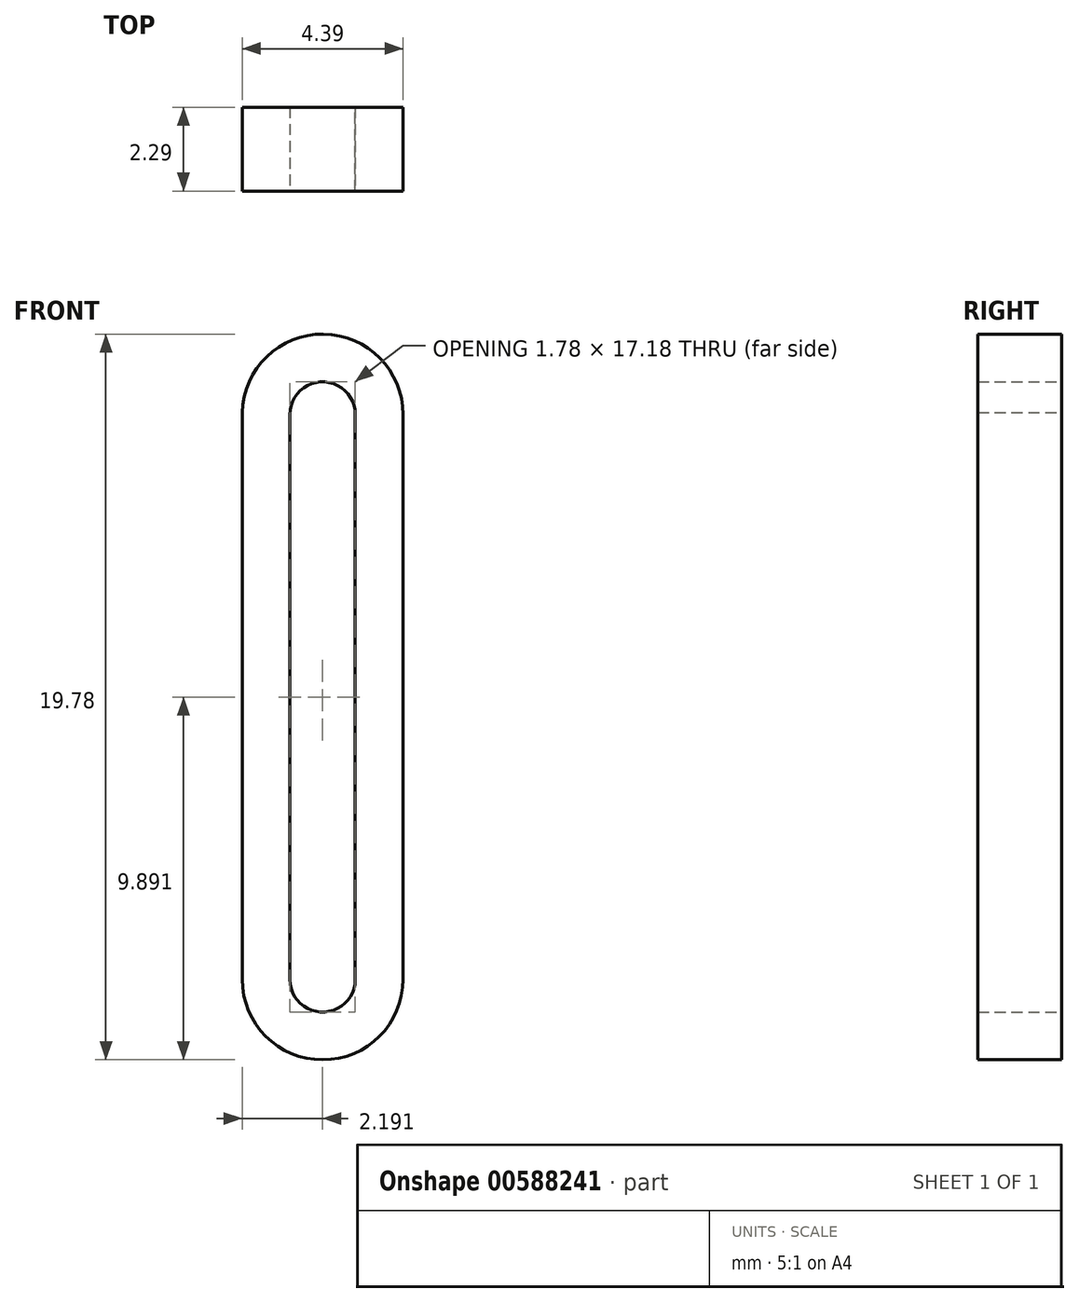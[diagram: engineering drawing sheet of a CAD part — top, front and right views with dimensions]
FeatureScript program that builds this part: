
annotation { "Feature Type Name" : "Feature", "Feature Type Description" : "" }
export const myFeature = defineFeature(function(context is Context, id is Id, definition is map)
    precondition{}
    {
        {
            var Q0;
            Q0=qCreatedBy(makeId("Front.planeOp"),FACE);
            var sketch = newSketch(context, id + "F0", { "sketchPlane" : qUnion([Q0])});
            skLineSegment(sketch, "E0", {"start": v(-49.36, 48.2) * mm, "end": v(-49.36, 32.75) * mm});
            skArc(sketch, "E1", {"start": v(-49.36, 32.75) * mm, "mid": v(-47.17, 30.56) * mm, "end": v(-44.97, 32.75) * mm});
            skLineSegment(sketch, "E2", {"start": v(-44.97, 32.75) * mm, "end": v(-44.97, 48.15) * mm});
            skArc(sketch, "E3", {"start": v(-44.97, 48.15) * mm, "mid": v(-47.14, 50.34) * mm, "end": v(-49.36, 48.2) * mm});
            skLineSegment(sketch, "E4", {"start": v(-46.28, 48.15) * mm, "end": v(-46.28, 32.75) * mm});
            skLineSegment(sketch, "E5", {"start": v(-48.06, 32.75) * mm, "end": v(-48.06, 48.15) * mm});
            skArc(sketch, "E6", {"start": v(-46.28, 48.15) * mm, "mid": v(-47.17, 49.04) * mm, "end": v(-48.06, 48.15) * mm});
            skArc(sketch, "E7", {"start": v(-48.06, 32.75) * mm, "mid": v(-47.17, 31.86) * mm, "end": v(-46.28, 32.75) * mm});
            skSolve(sketch);
        }
        {
            var Q0;
            Q0=makeQuery(id+"F0.imprint","IMPRINT",FACE,{"disambiguationData":[TD([[makeQuery(id+"F0.imprint","IMPRINT",EDGE,{"derivedFrom":sQuery(id+"F0.wireOp",EDGE,"E0")}),1.0]])]});
            extrude(context, id + "F1", {"entities" : qUnion([Q0]), "depth" : 2.3 * mm, "offsetDistance" : 25.4 * mm});
        }
        {
            var Q0;
            Q0=sQuery(id+"F0.wireOp",VERTEX,"E3.center");
            var Q1;
            Q1=sQuery(id+"F0.wireOp",VERTEX,"E1.center");
            var Q2;
            Q2=makeQuery(id+"F1.opExtrude","SWEPT_BODY",BODY,{"disambiguationData":[OSD([sQuery(id+"F0.wireOp",EDGE,"E0"),sQuery(id+"F0.wireOp",EDGE,"E1"),sQuery(id+"F0.wireOp",EDGE,"E2"),sQuery(id+"F0.wireOp",EDGE,"E3")])]});
            hole(context, id + "F2", {"style" : HoleStyle.SIMPLE, "endStyle" : HoleEndStyle.THROUGH, "oppositeDirection" : true, "holeDiameter" : 1.78 * mm, "majorDiameter" : 6.35 * mm, "isTappedThrough" : true, "tappedDepth" : 12.7 * mm, "tapClearance" : 3, "locations" : qUnion([Q0, Q1]), "scope" : qUnion([Q2])});
        }
    });
